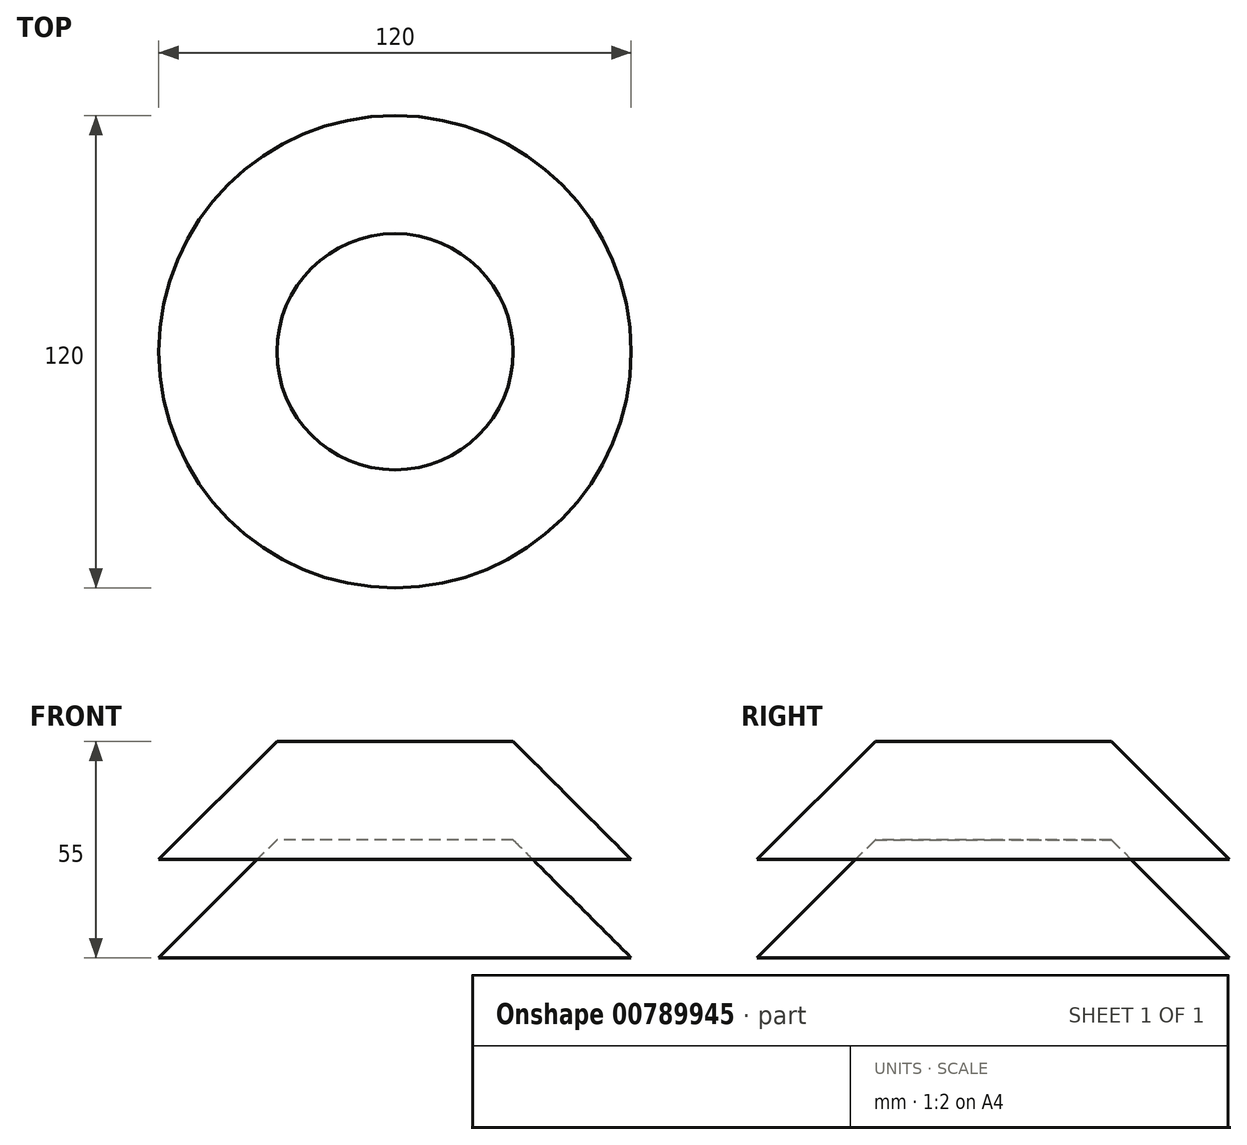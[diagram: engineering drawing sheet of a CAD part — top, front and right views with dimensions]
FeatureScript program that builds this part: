
annotation { "Feature Type Name" : "Feature", "Feature Type Description" : "" }
export const myFeature = defineFeature(function(context is Context, id is Id, definition is map)
    precondition{}
    {
        {
            var Q0;
            Q0=qCreatedBy(makeId("Top.planeOp"),FACE);
            var sketch = newSketch(context, id + "F0", { "sketchPlane" : qUnion([Q0])});
            skCircle(sketch, "E0", {"center": v(0, 0) * mm, "radius": 30 * mm});
            skSolve(sketch);
        }
        {
            var Q0;
            Q0=makeQuery(id+"F0.imprint","IMPRINT",FACE,{"disambiguationData":[TD([[makeQuery(id+"F0.imprint","IMPRINT",EDGE,{"derivedFrom":sQuery(id+"F0.wireOp",EDGE,"E0")}),1.0]])]});
            extrude(context, id + "F1", {"entities" : qUnion([Q0]), "oppositeDirection" : true, "depth" : 30 * mm, "offsetDistance" : 25 * mm, "hasDraft" : true, "draftAngle" : 45 * degree});
        }
        {
            var Q0;
            Q0=qCreatedBy(makeId("Top.planeOp"),FACE);
            cPlane(context, id + "F2", {"entities" : qUnion([Q0]), "cplaneType" : CPlaneType.OFFSET, "offset" : 25 * mm, "width" : 150 * mm, "height" : 150 * mm});
        }
        {
            var Q0;
            Q0=qCreatedBy(id+"F2.planeOp",FACE);
            var sketch = newSketch(context, id + "F3", { "sketchPlane" : qUnion([Q0])});
            skCircle(sketch, "E1.0", {"center": v(0, 0) * mm, "radius": 30 * mm});
            skSolve(sketch);
        }
        {
            var Q0;
            Q0=makeQuery(id+"F3.imprint","IMPRINT",FACE,{"disambiguationData":[TD([[makeQuery(id+"F3.imprint","IMPRINT",EDGE,{"derivedFrom":sQuery(id+"F3.wireOp",EDGE,"E1.0")}),1.0]])]});
            extrude(context, id + "F4", {"entities" : qUnion([Q0]), "oppositeDirection" : true, "depth" : 30 * mm, "offsetDistance" : 25 * mm, "hasDraft" : true, "draftAngle" : 45 * degree});
        }
    });
